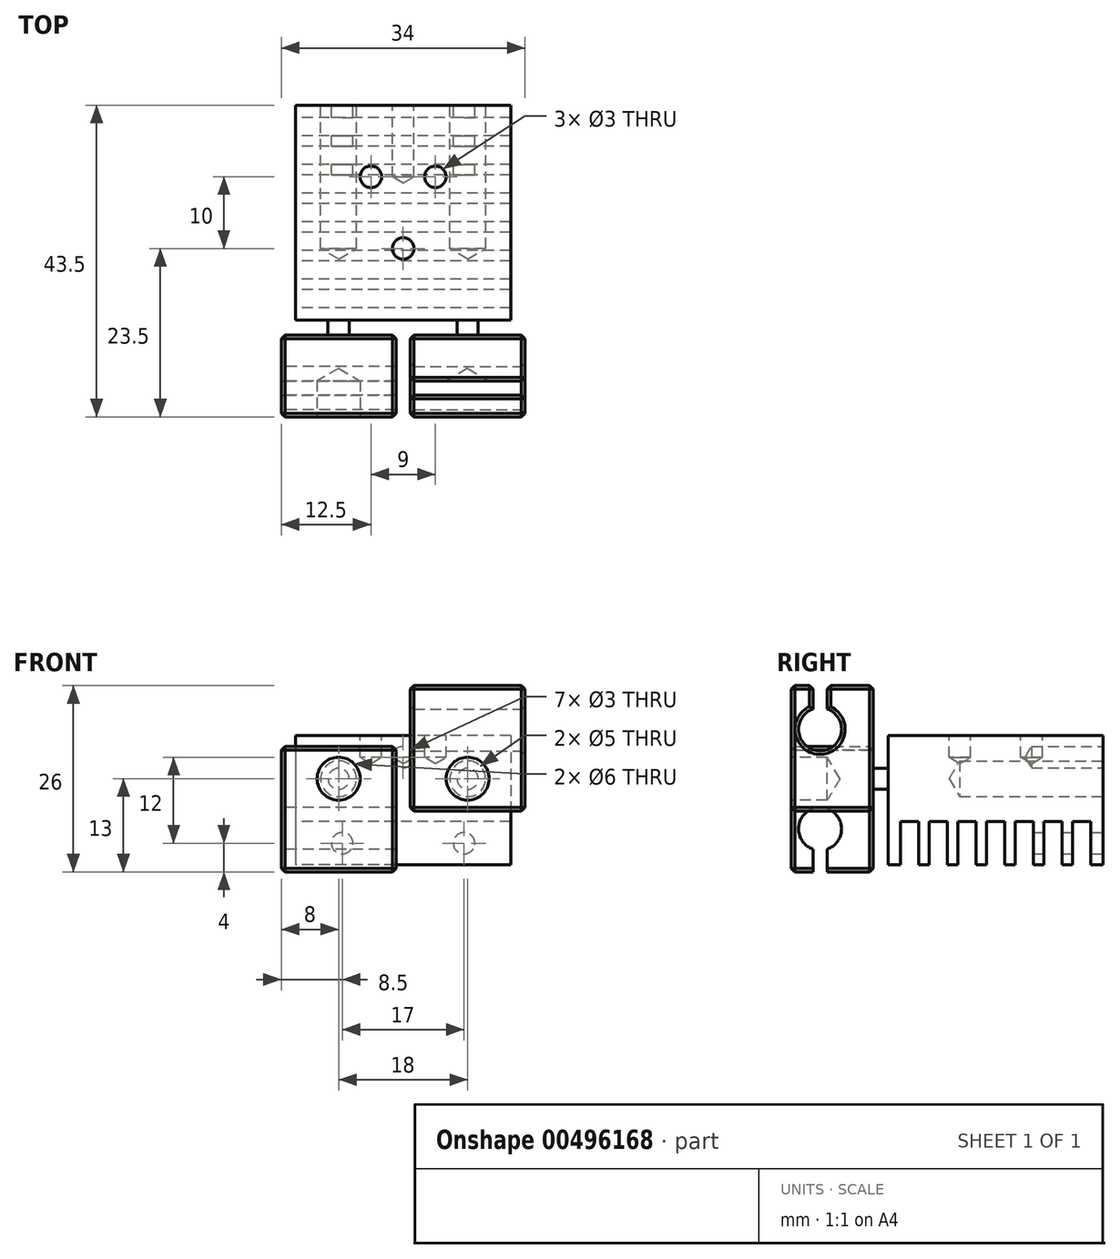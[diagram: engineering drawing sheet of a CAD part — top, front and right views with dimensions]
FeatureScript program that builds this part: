
annotation { "Feature Type Name" : "Feature", "Feature Type Description" : "" }
export const myFeature = defineFeature(function(context is Context, id is Id, definition is map)
    precondition{}
    {
        {
            var Q0;
            Q0=qCreatedBy(makeId("Top.planeOp"),FACE);
            var sketch = newSketch(context, id + "F0", { "sketchPlane" : qUnion([Q0])});
            skLineSegment(sketch, "E0.bottom", {"start": v(15, -15) * mm, "end": v(-15, -15) * mm});
            skLineSegment(sketch, "E0.top", {"start": v(15, 15) * mm, "end": v(-15, 15) * mm});
            skLineSegment(sketch, "E0.left", {"start": v(15, -15) * mm, "end": v(15, 15) * mm});
            skLineSegment(sketch, "E0.right", {"start": v(-15, -15) * mm, "end": v(-15, 15) * mm});
            skPoint(sketch, "E0.middle", {"position": v(0, 0) * mm});
            skSolve(sketch);
        }
        {
            var Q0;
            Q0=makeQuery(id+"F0.imprint","IMPRINT",FACE,{"disambiguationData":[TD([[makeQuery(id+"F0.imprint","IMPRINT",EDGE,{"derivedFrom":sQuery(id+"F0.wireOp",EDGE,"E0.bottom")}),-1.0]])]});
            extrude(context, id + "F10", {"entities" : qUnion([Q0]), "depth" : 18 * mm});
        }
        {
            var Q0;
            Q0=makeQuery(id+"F10.opExtrude","SWEPT_FACE",FACE,{"disambiguationData":[OSD([sQuery(id+"F0.wireOp",EDGE,"E0.top")])]});
            var sketch = newSketch(context, id + "F11", { "sketchPlane" : qUnion([Q0])});
            skPoint(sketch, "E1", {"position": v(-8.5, 3) * mm});
            skPoint(sketch, "E2", {"position": v(8.5, 3) * mm});
            skPoint(sketch, "E3", {"position": v(-9, 12) * mm});
            skPoint(sketch, "E4", {"position": v(9, 12) * mm});
            skPoint(sketch, "E5", {"position": v(0, 15) * mm});
            skSolve(sketch);
        }
        {
            var Q0;
            Q0=sQuery(id+"F11.wireOp",VERTEX,"E3");
            var Q1;
            Q1=sQuery(id+"F11.wireOp",VERTEX,"E4");
            var Q2;
            Q2=makeQuery(id+"F10.opExtrude","SWEPT_BODY",BODY,{"disambiguationData":[OSD([sQuery(id+"F0.wireOp",EDGE,"E0.bottom"),sQuery(id+"F0.wireOp",EDGE,"E0.top"),sQuery(id+"F0.wireOp",EDGE,"E0.left"),sQuery(id+"F0.wireOp",EDGE,"E0.right")])]});
            hole(context, id + "F1", {"style" : HoleStyle.SIMPLE, "endStyle" : HoleEndStyle.BLIND, "holeDiameter" : 5 * mm, "holeDepth" : 20 * mm, "locations" : qUnion([Q0, Q1]), "scope" : qUnion([Q2])});
        }
        {
            var Q0;
            Q0=makeQuery(id+"F10.opExtrude","CAP_FACE",FACE,{"disambiguationData":[OSD([sQuery(id+"F0.wireOp",EDGE,"E0.bottom"),sQuery(id+"F0.wireOp",EDGE,"E0.top"),sQuery(id+"F0.wireOp",EDGE,"E0.left"),sQuery(id+"F0.wireOp",EDGE,"E0.right")])],"isStart":true});
            var sketch = newSketch(context, id + "F12", { "sketchPlane" : qUnion([Q0])});
            skLineSegment(sketch, "E6.bottom", {"start": v(15, -13.25) * mm, "end": v(-15.01, -13.25) * mm});
            skLineSegment(sketch, "E6.top", {"start": v(15, -10.75) * mm, "end": v(-15.01, -10.75) * mm});
            skLineSegment(sketch, "E6.left", {"start": v(15, -13.25) * mm, "end": v(15, -10.75) * mm});
            skLineSegment(sketch, "E6.right", {"start": v(-15.01, -13.25) * mm, "end": v(-15.01, -10.75) * mm});
            skLineSegment(sketch, "E7.0.1.0", {"start": v(15, -9.25) * mm, "end": v(15, -6.75) * mm});
            skLineSegment(sketch, "E7.0.1.1", {"start": v(-15.01, -9.25) * mm, "end": v(-15.01, -6.75) * mm});
            skLineSegment(sketch, "E7.0.1.2", {"start": v(15, -9.25) * mm, "end": v(-15.01, -9.25) * mm});
            skLineSegment(sketch, "E7.0.1.3", {"start": v(15, -6.75) * mm, "end": v(-15.01, -6.75) * mm});
            skLineSegment(sketch, "E7.0.2.0", {"start": v(15, -5.25) * mm, "end": v(15, -2.75) * mm});
            skLineSegment(sketch, "E7.0.2.1", {"start": v(-15.01, -5.25) * mm, "end": v(-15.01, -2.75) * mm});
            skLineSegment(sketch, "E7.0.2.2", {"start": v(15, -5.25) * mm, "end": v(-15.01, -5.25) * mm});
            skLineSegment(sketch, "E7.0.2.3", {"start": v(15, -2.75) * mm, "end": v(-15.01, -2.75) * mm});
            skLineSegment(sketch, "E7.0.3.0", {"start": v(15, -1.25) * mm, "end": v(15, 1.25) * mm});
            skLineSegment(sketch, "E7.0.3.1", {"start": v(-15.01, -1.25) * mm, "end": v(-15.01, 1.25) * mm});
            skLineSegment(sketch, "E7.0.3.2", {"start": v(15, -1.25) * mm, "end": v(-15.01, -1.25) * mm});
            skLineSegment(sketch, "E7.0.3.3", {"start": v(15, 1.25) * mm, "end": v(-15.01, 1.25) * mm});
            skLineSegment(sketch, "E7.0.4.0", {"start": v(15, 2.75) * mm, "end": v(15, 5.25) * mm});
            skLineSegment(sketch, "E7.0.4.1", {"start": v(-15.01, 2.75) * mm, "end": v(-15.01, 5.25) * mm});
            skLineSegment(sketch, "E7.0.4.2", {"start": v(15, 2.75) * mm, "end": v(-15.01, 2.75) * mm});
            skLineSegment(sketch, "E7.0.4.3", {"start": v(15, 5.25) * mm, "end": v(-15.01, 5.25) * mm});
            skLineSegment(sketch, "E7.0.5.0", {"start": v(15, 6.75) * mm, "end": v(15, 9.25) * mm});
            skLineSegment(sketch, "E7.0.5.1", {"start": v(-15.01, 6.75) * mm, "end": v(-15.01, 9.25) * mm});
            skLineSegment(sketch, "E7.0.5.2", {"start": v(15, 6.75) * mm, "end": v(-15.01, 6.75) * mm});
            skLineSegment(sketch, "E7.0.5.3", {"start": v(15, 9.25) * mm, "end": v(-15.01, 9.25) * mm});
            skLineSegment(sketch, "E7.0.6.0", {"start": v(15, 10.75) * mm, "end": v(15, 13.25) * mm});
            skLineSegment(sketch, "E7.0.6.1", {"start": v(-15.01, 10.75) * mm, "end": v(-15.01, 13.25) * mm});
            skLineSegment(sketch, "E7.0.6.2", {"start": v(15, 10.75) * mm, "end": v(-15.01, 10.75) * mm});
            skLineSegment(sketch, "E7.0.6.3", {"start": v(15, 13.25) * mm, "end": v(-15.01, 13.25) * mm});
            skLineSegment(sketch, "E7.direction1", {"start": v(-15.01, -13.25) * mm, "end": v(9.99, -13.25) * mm, "construction": true});
            skLineSegment(sketch, "E7.direction2", {"start": v(-15.01, -13.25) * mm, "end": v(-15.01, -9.25) * mm, "construction": true});
            skSolve(sketch);
        }
        {
            var Q0;
            {var subQ0=sQuery(id+"F12.wireOp",EDGE,"E7.0.6.0");Q0=makeQuery(id+"F12.imprint","IMPRINT",FACE,{"disambiguationData":[TD([[makeQuery(id+"F12.imprint","IMPRINT",EDGE,{"derivedFrom":subQ0}),-1.0]])]});}
            var Q1;
            {var subQ0=sQuery(id+"F12.wireOp",EDGE,"E7.0.5.0");Q1=makeQuery(id+"F12.imprint","IMPRINT",FACE,{"disambiguationData":[TD([[makeQuery(id+"F12.imprint","IMPRINT",EDGE,{"derivedFrom":subQ0}),-1.0]])]});}
            var Q2;
            {var subQ0=sQuery(id+"F12.wireOp",EDGE,"E7.0.4.0");Q2=makeQuery(id+"F12.imprint","IMPRINT",FACE,{"disambiguationData":[TD([[makeQuery(id+"F12.imprint","IMPRINT",EDGE,{"derivedFrom":subQ0}),-1.0]])]});}
            var Q3;
            {var subQ0=sQuery(id+"F12.wireOp",EDGE,"E7.0.3.0");Q3=makeQuery(id+"F12.imprint","IMPRINT",FACE,{"disambiguationData":[TD([[makeQuery(id+"F12.imprint","IMPRINT",EDGE,{"derivedFrom":subQ0}),-1.0]])]});}
            var Q4;
            {var subQ0=sQuery(id+"F12.wireOp",EDGE,"E7.0.2.0");Q4=makeQuery(id+"F12.imprint","IMPRINT",FACE,{"disambiguationData":[TD([[makeQuery(id+"F12.imprint","IMPRINT",EDGE,{"derivedFrom":subQ0}),-1.0]])]});}
            var Q5;
            {var subQ0=sQuery(id+"F12.wireOp",EDGE,"E7.0.1.0");Q5=makeQuery(id+"F12.imprint","IMPRINT",FACE,{"disambiguationData":[TD([[makeQuery(id+"F12.imprint","IMPRINT",EDGE,{"derivedFrom":subQ0}),-1.0]])]});}
            var Q6;
            {var subQ0=sQuery(id+"F12.wireOp",EDGE,"E6.left");Q6=makeQuery(id+"F12.imprint","IMPRINT",FACE,{"disambiguationData":[TD([[makeQuery(id+"F12.imprint","IMPRINT",EDGE,{"derivedFrom":subQ0}),-1.0]])]});}
            extrude(context, id + "F13", {"entities" : qUnion([Q0, Q1, Q2, Q3, Q4, Q5, Q6]), "operationType" : NewBodyOperationType.REMOVE, "oppositeDirection" : true, "depth" : 6 * mm});
        }
        {
            var Q0;
            Q0=makeQuery(id+"F10.opExtrude","CAP_FACE",FACE,{"disambiguationData":[OSD([sQuery(id+"F0.wireOp",EDGE,"E0.bottom"),sQuery(id+"F0.wireOp",EDGE,"E0.top"),sQuery(id+"F0.wireOp",EDGE,"E0.left"),sQuery(id+"F0.wireOp",EDGE,"E0.right")])],"isStart":false});
            var sketch = newSketch(context, id + "F2", { "sketchPlane" : qUnion([Q0])});
            skPoint(sketch, "E8", {"position": v(-4.5, 5) * mm});
            skPoint(sketch, "E9", {"position": v(4.5, 5) * mm});
            skPoint(sketch, "E10", {"position": v(0, -5) * mm});
            skSolve(sketch);
        }
        {
            var Q0;
            Q0=sQuery(id+"F2.wireOp",VERTEX,"E9");
            var Q1;
            Q1=sQuery(id+"F2.wireOp",VERTEX,"E8");
            var Q2;
            Q2=sQuery(id+"F2.wireOp",VERTEX,"E10");
            var Q3;
            Q3=makeQuery(id+"F10.opExtrude","SWEPT_BODY",BODY,{"disambiguationData":[OSD([sQuery(id+"F0.wireOp",EDGE,"E0.bottom"),sQuery(id+"F0.wireOp",EDGE,"E0.top"),sQuery(id+"F0.wireOp",EDGE,"E0.left"),sQuery(id+"F0.wireOp",EDGE,"E0.right")])]});
            hole(context, id + "F14", {"style" : HoleStyle.SIMPLE, "endStyle" : HoleEndStyle.BLIND, "holeDiameter" : 3 * mm, "holeDepth" : 3 * mm, "locations" : qUnion([Q0, Q1, Q2]), "scope" : qUnion([Q3])});
        }
        {
            var Q0;
            Q0=sQuery(id+"F11.wireOp",VERTEX,"E2");
            var Q1;
            Q1=sQuery(id+"F11.wireOp",VERTEX,"E1");
            var Q2;
            Q2=sQuery(id+"F11.wireOp",VERTEX,"E5");
            var Q3;
            Q3=makeQuery(id+"F10.opExtrude","SWEPT_BODY",BODY,{"disambiguationData":[OSD([sQuery(id+"F0.wireOp",EDGE,"E0.bottom"),sQuery(id+"F0.wireOp",EDGE,"E0.top"),sQuery(id+"F0.wireOp",EDGE,"E0.left"),sQuery(id+"F0.wireOp",EDGE,"E0.right")])]});
            hole(context, id + "F15", {"style" : HoleStyle.SIMPLE, "endStyle" : HoleEndStyle.BLIND, "holeDiameter" : 3 * mm, "holeDepth" : 10 * mm, "locations" : qUnion([Q0, Q1, Q2]), "scope" : qUnion([Q3])});
        }
        {
            var Q0;
            Q0=makeQuery(id+"F10.opExtrude","SWEPT_FACE",FACE,{"disambiguationData":[OSD([sQuery(id+"F0.wireOp",EDGE,"E0.bottom")])]});
            var sketch = newSketch(context, id + "F3", { "sketchPlane" : qUnion([Q0])});
            skCircle(sketch, "E11", {"center": v(9, 12) * mm, "radius": 1.48 * mm});
            skCircle(sketch, "E12", {"center": v(-9, 12) * mm, "radius": 1.48 * mm});
            skSolve(sketch);
        }
        {
            var Q0;
            Q0=makeQuery(id+"F3.imprint","IMPRINT",FACE,{"disambiguationData":[TD([[makeQuery(id+"F3.imprint","IMPRINT",EDGE,{"derivedFrom":sQuery(id+"F3.wireOp",EDGE,"E12")}),1.0]])]});
            var Q1;
            Q1=makeQuery(id+"F3.imprint","IMPRINT",FACE,{"disambiguationData":[TD([[makeQuery(id+"F3.imprint","IMPRINT",EDGE,{"derivedFrom":sQuery(id+"F3.wireOp",EDGE,"E11")}),1.0]])]});
            extrude(context, id + "F4", {"entities" : qUnion([Q0, Q1]), "operationType" : NewBodyOperationType.ADD, "depth" : 2.1 * mm});
        }
        {
            var Q0;
            Q0=makeQuery(id+"F4.opExtrude","CAP_FACE",FACE,{"disambiguationData":[OSD([sQuery(id+"F3.wireOp",EDGE,"E11")])],"isStart":false});
            var sketch = newSketch(context, id + "F16", { "sketchPlane" : qUnion([Q0])});
            skLineSegment(sketch, "E13.bottom", {"start": v(1, 25) * mm, "end": v(17, 25) * mm});
            skLineSegment(sketch, "E13.top", {"start": v(1, 7.5) * mm, "end": v(17, 7.5) * mm});
            skLineSegment(sketch, "E13.left", {"start": v(1, 25) * mm, "end": v(1, 7.5) * mm});
            skLineSegment(sketch, "E13.right", {"start": v(17, 25) * mm, "end": v(17, 7.5) * mm});
            skPoint(sketch, "E14", {"position": v(9, 12) * mm});
            skSolve(sketch);
        }
        {
            var Q0;
            Q0=makeQuery(id+"F4.opExtrude","CAP_FACE",FACE,{"disambiguationData":[OSD([sQuery(id+"F3.wireOp",EDGE,"E12")])],"isStart":false});
            var sketch = newSketch(context, id + "F17", { "sketchPlane" : qUnion([Q0])});
            skPoint(sketch, "E15", {"position": v(-9, 12) * mm});
            skLineSegment(sketch, "E16.bottom", {"start": v(-17, 16.5) * mm, "end": v(-1, 16.5) * mm});
            skLineSegment(sketch, "E16.top", {"start": v(-17, -1) * mm, "end": v(-1, -1) * mm});
            skLineSegment(sketch, "E16.left", {"start": v(-17, 16.5) * mm, "end": v(-17, -1) * mm});
            skLineSegment(sketch, "E16.right", {"start": v(-1, 16.5) * mm, "end": v(-1, -1) * mm});
            skSolve(sketch);
        }
        {
            var Q0;
            Q0=qSketchRegion(id+"F17",true);
            var Q1;
            Q1=qSketchRegion(id+"F16",true);
            extrude(context, id + "F18", {"entities" : qUnion([Q0, Q1]), "operationType" : NewBodyOperationType.ADD, "depth" : 11.4 * mm});
        }
        {
            var Q0;
            Q0=makeQuery(id+"F18.opExtrude","CAP_FACE",FACE,{"disambiguationData":[OSD([sQuery(id+"F16.wireOp",EDGE,"E13.bottom"),sQuery(id+"F16.wireOp",EDGE,"E13.top"),sQuery(id+"F16.wireOp",EDGE,"E13.left"),sQuery(id+"F16.wireOp",EDGE,"E13.right")])],"isStart":false});
            var sketch = newSketch(context, id + "F19", { "sketchPlane" : qUnion([Q0])});
            skPoint(sketch, "E17", {"position": v(9, 12) * mm});
            skPoint(sketch, "E17.positionSnap0", {"position": v(9, 7.5) * mm});
            skSolve(sketch);
        }
        {
            var Q0;
            Q0=makeQuery(id+"F18.opExtrude","CAP_FACE",FACE,{"disambiguationData":[OSD([sQuery(id+"F17.wireOp",EDGE,"E16.bottom"),sQuery(id+"F17.wireOp",EDGE,"E16.top"),sQuery(id+"F17.wireOp",EDGE,"E16.left"),sQuery(id+"F17.wireOp",EDGE,"E16.right")])],"isStart":false});
            var sketch = newSketch(context, id + "F20", { "sketchPlane" : qUnion([Q0])});
            skPoint(sketch, "E18", {"position": v(-9, 12) * mm});
            skPoint(sketch, "E18.positionSnap0", {"position": v(-9, 16.5) * mm});
            skSolve(sketch);
        }
        {
            var Q0;
            Q0=sQuery(id+"F20.wireOp",VERTEX,"E18");
            var Q1;
            Q1=sQuery(id+"F19.wireOp",VERTEX,"E17");
            var Q2;
            Q2=makeQuery(id+"F10.opExtrude","SWEPT_BODY",BODY,{"disambiguationData":[OSD([sQuery(id+"F0.wireOp",EDGE,"E0.bottom"),sQuery(id+"F0.wireOp",EDGE,"E0.top"),sQuery(id+"F0.wireOp",EDGE,"E0.left"),sQuery(id+"F0.wireOp",EDGE,"E0.right")])]});
            hole(context, id + "F5", {"style" : HoleStyle.SIMPLE, "endStyle" : HoleEndStyle.BLIND, "holeDiameter" : 6 * mm, "holeDepth" : 5 * mm, "locations" : qUnion([Q0, Q1]), "scope" : qUnion([Q2])});
        }
        {
            var Q0;
            Q0=makeQuery(id+"F18.opExtrude","SWEPT_FACE",FACE,{"disambiguationData":[OSD([sQuery(id+"F16.wireOp",EDGE,"E13.right")])]});
            var sketch = newSketch(context, id + "F6", { "sketchPlane" : qUnion([Q0])});
            skArc(sketch, "E19", {"start": v(-25.5, 21.73) * mm, "mid": v(-24.5, 15.9) * mm, "end": v(-23.5, 21.73) * mm});
            skLineSegment(sketch, "E20.bottom", {"start": v(-25.5, 30.74) * mm, "end": v(-23.5, 30.74) * mm});
            skLineSegment(sketch, "E20.top", {"start": v(-25.5, 7.06) * mm, "end": v(-23.5, 7.06) * mm});
            skLineSegment(sketch, "E20.left", {"start": v(-25.5, 30.74) * mm, "end": v(-25.5, 21.73) * mm});
            skLineSegment(sketch, "E20.right", {"start": v(-23.5, 30.74) * mm, "end": v(-23.5, 21.73) * mm});
            skSolve(sketch);
        }
        {
            var Q0;
            {var subQ0=sQuery(id+"F6.wireOp",EDGE,"E19");Q0=makeQuery(id+"F6.imprint","IMPRINT",FACE,{"disambiguationData":[TD([[makeQuery(id+"F6.imprint","IMPRINT",EDGE,{"derivedFrom":subQ0}),1.0]])]});}
            extrude(context, id + "F7", {"entities" : qUnion([Q0]), "operationType" : NewBodyOperationType.REMOVE, "endBound" : BoundingType.UP_TO_NEXT, "oppositeDirection" : true, "depth" : 25 * mm});
        }
        {
            var Q0;
            Q0=makeQuery(id+"F18.opExtrude","SWEPT_FACE",FACE,{"disambiguationData":[OSD([sQuery(id+"F16.wireOp",EDGE,"E13.right")])]});
            var Q1;
            Q1=makeQuery(id+"F18.opExtrude","SWEPT_FACE",FACE,{"disambiguationData":[OSD([sQuery(id+"F16.wireOp",EDGE,"E13.top")])]});
            var Q2;
            Q2=makeQuery(id+"F18.opExtrude","SWEPT_FACE",FACE,{"disambiguationData":[OSD([sQuery(id+"F17.wireOp",EDGE,"E16.top")])]});
            var Q3;
            Q3=makeQuery(id+"F18.opExtrude","SWEPT_FACE",FACE,{"disambiguationData":[OSD([sQuery(id+"F17.wireOp",EDGE,"E16.right")])]});
            var Q4;
            {var subQ2=sQuery(id+"F16.wireOp",EDGE,"E13.bottom");Q4=makeQuery(id+"F7.boolean.opBoolean","SPLIT",FACE,{"disambiguationData":[TD([makeQuery(id+"F7.opExtrude","SWEPT_FACE",FACE,{"disambiguationData":[OSD([sQuery(id+"F6.wireOp",EDGE,"E20.right")])]})])],"derivedFrom":makeQuery(id+"F18.opExtrude","SWEPT_FACE",FACE,{"disambiguationData":[OSD([subQ2])]})});}
            var Q5;
            {var subQ2=sQuery(id+"F16.wireOp",EDGE,"E13.bottom");Q5=makeQuery(id+"F7.boolean.opBoolean","SPLIT",FACE,{"disambiguationData":[TD([makeQuery(id+"F7.opExtrude","SWEPT_FACE",FACE,{"disambiguationData":[OSD([sQuery(id+"F6.wireOp",EDGE,"E20.left")])]})])],"derivedFrom":makeQuery(id+"F18.opExtrude","SWEPT_FACE",FACE,{"disambiguationData":[OSD([subQ2])]})});}
            var Q6;
            Q6=makeQuery(id+"F18.opExtrude","SWEPT_FACE",FACE,{"disambiguationData":[OSD([sQuery(id+"F17.wireOp",EDGE,"E16.bottom")])]});
            var Q7;
            Q7=makeQuery(id+"F18.opExtrude","SWEPT_FACE",FACE,{"disambiguationData":[OSD([sQuery(id+"F17.wireOp",EDGE,"E16.left")])]});
            var Q8;
            Q8=makeQuery(id+"F18.opExtrude","SWEPT_FACE",FACE,{"disambiguationData":[OSD([sQuery(id+"F16.wireOp",EDGE,"E13.left")])]});
            chamfer(context, id + "F8", {"entities" : qUnion([Q0, Q1, Q2, Q3, Q4, Q5, Q6, Q7, Q8]), "width" : 0.5 * mm, "tangentPropagation" : true});
        }
        {
            var Q0;
            Q0=makeQuery(id+"F18.opExtrude","SWEPT_FACE",FACE,{"disambiguationData":[OSD([sQuery(id+"F17.wireOp",EDGE,"E16.left")])]});
            var sketch = newSketch(context, id + "F9", { "sketchPlane" : qUnion([Q0])});
            skArc(sketch, "E21", {"start": v(25.5, 2.17) * mm, "mid": v(24.5, 8) * mm, "end": v(23.5, 2.17) * mm});
            skLineSegment(sketch, "E22.top", {"start": v(25.5, -1.5) * mm, "end": v(23.5, -1.5) * mm});
            skLineSegment(sketch, "E22.left", {"start": v(25.5, 11.5) * mm, "end": v(25.5, 7.83) * mm});
            skLineSegment(sketch, "E22.right", {"start": v(23.5, 2.17) * mm, "end": v(23.5, -1.5) * mm});
            skPoint(sketch, "E23.orphan", {"position": v(23.5, 11.5) * mm});
            skLineSegment(sketch, "E24.trimOffspring", {"start": v(25.5, 2.17) * mm, "end": v(25.5, -1.5) * mm});
            skSolve(sketch);
        }
        {
            var Q0;
            {var subQ1=sQuery(id+"F9.wireOp",EDGE,"E21");var subQ9=makeQuery(id+"F9.imprint","IMPRINT",VERTEX,{"derivedFrom":subQ1});Q0=makeQuery(id+"F9.imprint","IMPRINT",FACE,{"disambiguationData":[TD([[makeQuery(id+"F9.imprint","IMPRINT",EDGE,{"disambiguationData":[TD([[subQ9,1.0]])],"derivedFrom":subQ1}),1.0]])]});}
            var Q1;
            {var subQ0=sQuery(id+"F9.wireOp",EDGE,"E22.top");Q1=makeQuery(id+"F9.imprint","IMPRINT",FACE,{"disambiguationData":[TD([[makeQuery(id+"F9.imprint","IMPRINT",EDGE,{"derivedFrom":subQ0}),-1.0]])]});}
            extrude(context, id + "F21", {"entities" : qUnion([Q0, Q1]), "operationType" : NewBodyOperationType.REMOVE, "endBound" : BoundingType.UP_TO_NEXT, "oppositeDirection" : true, "depth" : 25 * mm});
        }
    });
